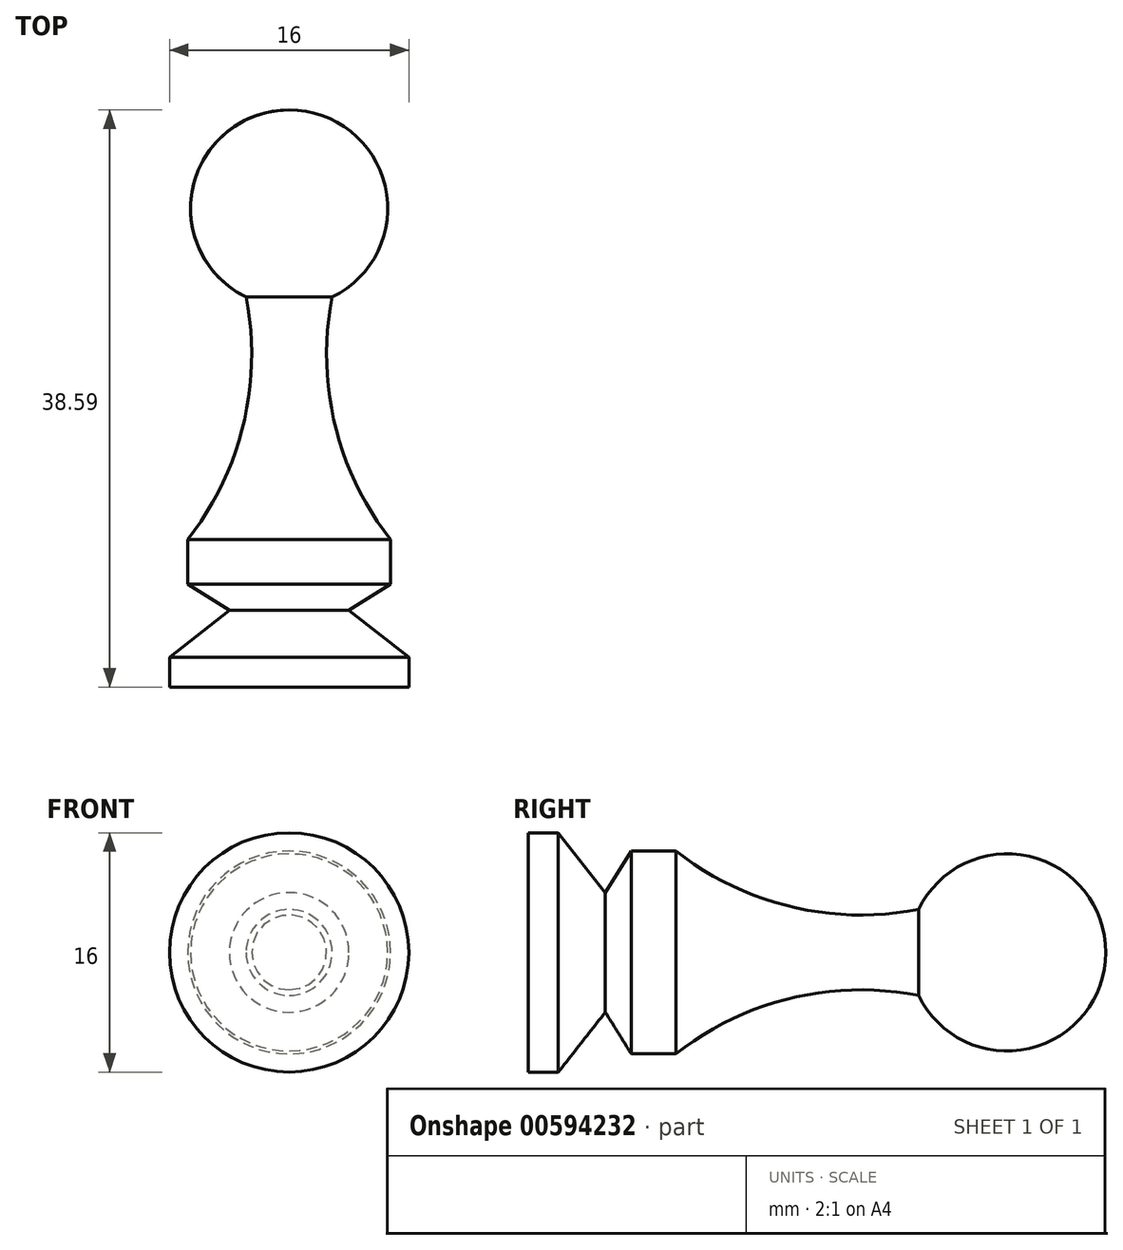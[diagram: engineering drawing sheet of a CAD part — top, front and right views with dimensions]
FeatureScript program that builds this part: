
annotation { "Feature Type Name" : "Feature", "Feature Type Description" : "" }
export const myFeature = defineFeature(function(context is Context, id is Id, definition is map)
    precondition{}
    {
        {
            var Q0;
            Q0=qCreatedBy(makeId("Top.planeOp"),FACE);
            var sketch = newSketch(context, id + "F0", { "sketchPlane" : qUnion([Q0])});
            skLineSegment(sketch, "E0", {"start": v(0, 0) * mm, "end": v(0, 32) * mm});
            skArc(sketch, "E1", {"start": v(0, 38.59) * mm, "mid": v(-6.42, 33.47) * mm, "end": v(-2.87, 26.07) * mm});
            skLineSegment(sketch, "E2", {"start": v(-2.87, 26.07) * mm, "end": v(0, 26.07) * mm});
            skLineSegment(sketch, "E3", {"start": v(0, 0) * mm, "end": v(-8, 0) * mm});
            skLineSegment(sketch, "E4", {"start": v(-8, 0) * mm, "end": v(-8, 2) * mm});
            skLineSegment(sketch, "E5", {"start": v(-8, 2) * mm, "end": v(-4, 5.14) * mm});
            skLineSegment(sketch, "E6", {"start": v(-4, 5.14) * mm, "end": v(-6.78, 6.87) * mm});
            skLineSegment(sketch, "E7", {"start": v(-6.78, 6.87) * mm, "end": v(-6.78, 9.87) * mm});
            skArc(sketch, "E8", {"start": v(-6.78, 9.87) * mm, "mid": v(-3.06, 17.54) * mm, "end": v(-2.87, 26.07) * mm});
            skLineSegment(sketch, "E9", {"start": v(0, 0) * mm, "end": v(0, 38.59) * mm});
            skSolve(sketch);
        }
        {
            var Q0;
            {var subQ0=sQuery(id+"F0.wireOp",EDGE,"E1");Q0=makeQuery(id+"F0.imprint","IMPRINT",FACE,{"disambiguationData":[TD([[makeQuery(id+"F0.imprint","IMPRINT",EDGE,{"derivedFrom":subQ0}),1.0]])]});}
            var Q1;
            {var subQ1=sQuery(id+"F0.wireOp",EDGE,"E2");Q1=makeQuery(id+"F0.imprint","IMPRINT",FACE,{"disambiguationData":[TD([[makeQuery(id+"F0.imprint","IMPRINT",EDGE,{"derivedFrom":subQ1}),-1.0]])]});}
            var Q2;
            Q2=sQuery(id+"F0.wireOp",EDGE,"E9");
            revolve(context, id + "F1", {"entities" : qUnion([Q0, Q1]), "axis" : qUnion([Q2]), "revolveType" : RevolveType.FULL});
        }
    });
